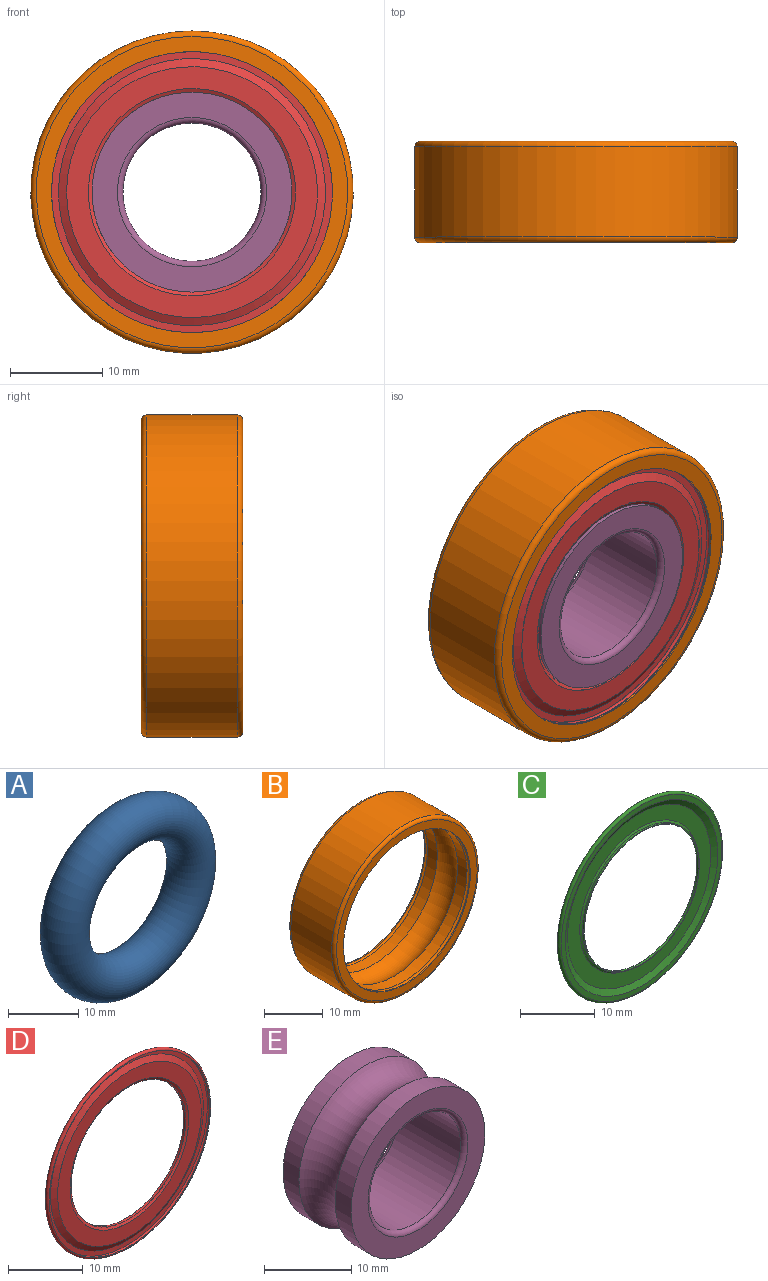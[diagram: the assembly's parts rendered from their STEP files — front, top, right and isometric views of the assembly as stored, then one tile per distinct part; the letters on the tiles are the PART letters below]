
ASSEMBLY  parts=5 mates=8
PART A: 1 faces, bbox 35.2x7x35.2 mm
  f0: torus R=12.75mm, axis (0,-1,0), area 1761.7mm2
PART B: 12 faces, bbox 37.9x11x37.9 mm
  f0: torus R=12.75mm, axis (0,-1,0), area 542.4mm2, adj f1,f9
  f1: cylinder r=15.25mm len=30.5mm, axis (0,-1,0), area 218.5mm2, adj f0,f2
  f2: torus R=15.25mm, axis (0,-1,0), area 91.4mm2, adj f1,f3
  f3: cylinder r=15.25mm len=30.5mm, axis (0,-1,0), area 16.3mm2, adj f2,f4
  f4: plane 33.8x33.8mm, normal (0,1,0), area 166.7mm2, adj f3,f10
  f5: cylinder r=17.5mm len=35mm, axis (0,-1,0), area 1077.6mm2, adj f10,f11
  f6: plane 33.8x33.8mm, normal (0,-1,0), area 166.7mm2, adj f7,f11
  f7: cylinder r=15.25mm len=30.5mm, axis (0,-1,0), area 16.3mm2, adj f6,f8
  f8: torus R=15.25mm, axis (0,-1,0), area 91.4mm2, adj f7,f9
  f9: cylinder r=15.25mm len=30.5mm, axis (0,-1,0), area 218.5mm2, adj f0,f8
  f10: torus R=16.9mm, axis (0,1,0), area 102.3mm2, adj f4,f5
  f11: torus R=16.9mm, axis (0,1,0), area 102.3mm2, adj f5,f6
PART C: 14 faces, bbox 33.7x0.6x33.7 mm
  f0: plane 21.9x21.9mm, normal (0,-1,0), area 6.8mm2, adj f7,f13
  f1: cylinder r=15.25mm len=30.5mm, axis (0,-1,0), area 9.6mm2, adj f2,f8
  f2: torus R=15.25mm, axis (0,-1,0), area 91.4mm2, adj f1,f3
  f3: plane 30.5x30.5mm, normal (0,-1,0), area 72.8mm2, adj f2,f4
  f4: cone r=13.59mm half-angle=61.9deg, axis (0,-1,0), area 87.9mm2, adj f3,f5
  f5: plane 27.18x27.18mm, normal (0,-1,0), area 181.2mm2, adj f4,f6
  f6: cone r=10.95mm half-angle=62deg, axis (0,1,0), area 25.3mm2, adj f5,f7
  f7: cylinder r=10.95mm len=21.9mm, axis (0,-1,0), area 20.6mm2, adj f0,f6
  f8: torus R=15.25mm, axis (0,-1,0), area 60.7mm2, adj f1,f9
  f9: plane 30.5x30.5mm, normal (0,1,0), area 70.5mm2, adj f8,f10
  f10: cone r=13.64mm half-angle=61.9deg, axis (0,-1,0), area 88.1mm2, adj f9,f11
  f11: plane 27.23x27.23mm, normal (0,1,0), area 185.1mm2, adj f10,f12
  f12: cone r=10.9mm half-angle=62deg, axis (0,1,0), area 31.1mm2, adj f11,f13
  f13: cylinder r=10.85mm len=21.7mm, axis (0,-1,0), area 24.5mm2, adj f0,f12
PART D: 14 faces, bbox 33.7x0.6x33.7 mm
  f0: plane 21.9x21.9mm, normal (0,1,0), area 6.8mm2, adj f7,f13
  f1: cylinder r=15.25mm len=30.5mm, axis (0,1,0), area 9.6mm2, adj f2,f8
  f2: torus R=15.25mm, axis (0,1,0), area 91.4mm2, adj f1,f3
  f3: plane 30.5x30.5mm, normal (0,1,0), area 72.8mm2, adj f2,f4
  f4: cone r=13.59mm half-angle=61.9deg, axis (0,1,0), area 87.9mm2, adj f3,f5
  f5: plane 27.18x27.18mm, normal (0,1,0), area 181.2mm2, adj f4,f6
  f6: cone r=10.95mm half-angle=62deg, axis (0,-1,0), area 25.3mm2, adj f5,f7
  f7: cylinder r=10.95mm len=21.9mm, axis (0,1,0), area 20.6mm2, adj f0,f6
  f8: torus R=15.25mm, axis (0,1,0), area 60.7mm2, adj f1,f9
  f9: plane 30.5x30.5mm, normal (0,-1,0), area 70.5mm2, adj f8,f10
  f10: cone r=13.64mm half-angle=61.9deg, axis (0,1,0), area 88.1mm2, adj f9,f11
  f11: plane 27.23x27.23mm, normal (0,-1,0), area 185.1mm2, adj f10,f12
  f12: cone r=10.9mm half-angle=62deg, axis (0,-1,0), area 31.1mm2, adj f11,f13
  f13: cylinder r=10.85mm len=21.7mm, axis (0,1,0), area 24.5mm2, adj f0,f12
PART E: 8 faces, bbox 27.6x11x27.6 mm
  f0: plane 21.7x21.7mm, normal (0,-1,0), area 163.7mm2, adj f5,f6
  f1: cylinder r=7.5mm len=15mm, axis (0,-1,0), area 461.8mm2, adj f6,f7
  f2: plane 21.7x21.7mm, normal (0,1,0), area 163.7mm2, adj f3,f7
  f3: cylinder r=10.85mm len=21.7mm, axis (0,-1,0), area 174.6mm2, adj f2,f4
  f4: torus R=12.75mm, axis (0,-1,0), area 429.8mm2, adj f3,f5
  f5: cylinder r=10.85mm len=21.7mm, axis (0,-1,0), area 174.6mm2, adj f0,f4
  f6: torus R=8.1mm, axis (0,1,0), area 45.7mm2, adj f0,f1
  f7: torus R=8.1mm, axis (0,1,0), area 45.7mm2, adj f1,f2
PLACE A at identity
PLACE B at identity
PLACE C rot(axis=(0,1,0),2.8deg) t=(0,0,0)mm
PLACE D rot(axis=(0,1,0),2.8deg) t=(0,0,0)mm
PLACE E at identity fixed
MATE ball B.f0 <-> C.f1  axis (0,-1,0) through (0,5.03,0)mm
MATE planar B.f0 <-> E.f1  axis (0,-1,0) through (0,0,0)mm
MATE ball B.f0 <-> A.f0  axis (0,-1,0) through (0,0,0)mm
MATE ball D.f1 <-> B.f0  axis (0,1,0) through (0,-5.03,0)mm
MATE parallel C.f1 <-> E.f1  axis (0,1,0) through (0,5.3,0)mm
MATE ball A.f0 <-> E.f1  axis (0,-1,0) through (0,0,0)mm
MATE planar A.f0 <-> E.f1  axis (0,-1,0) through (0,0,0)mm
MATE parallel D.f1 <-> E.f1  axis (0,-1,0) through (0,-5.3,0)mm
